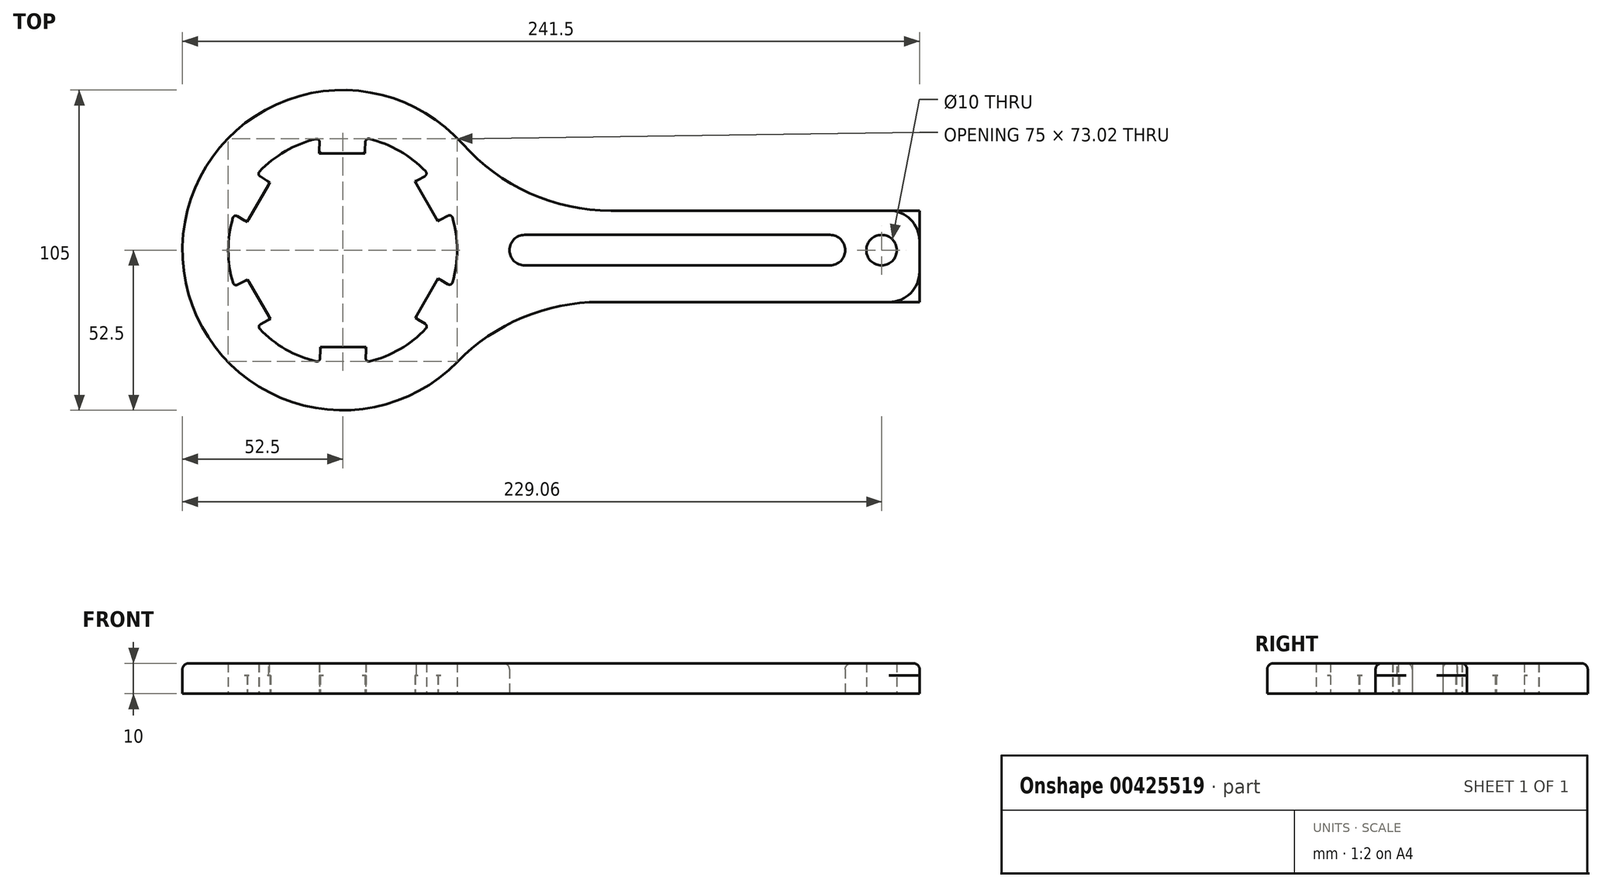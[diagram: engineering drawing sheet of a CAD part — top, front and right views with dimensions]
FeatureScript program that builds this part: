
annotation { "Feature Type Name" : "Feature", "Feature Type Description" : "" }
export const myFeature = defineFeature(function(context is Context, id is Id, definition is map)
    precondition{}
    {
        {
            var Q0;
            Q0=qCreatedBy(makeId("Top.planeOp"),FACE);
            var sketch = newSketch(context, id + "F0", { "sketchPlane" : qUnion([Q0])});
            skArc(sketch, "E0", {"start": v(-7.53, 36.74) * mm, "mid": v(-18.77, 32.46) * mm, "end": v(-28.09, 24.85) * mm});
            skArc(sketch, "E1", {"start": v(39.27, 34.84) * mm, "mid": v(-52.49, 1.23) * mm, "end": v(37.6, -36.65) * mm});
            skLineSegment(sketch, "E2.bottom", {"start": v(87.9, 12.98) * mm, "end": v(189, 12.98) * mm});
            skLineSegment(sketch, "E2.top", {"start": v(84.14, -17.02) * mm, "end": v(189, -17.02) * mm});
            skLineSegment(sketch, "E2.right", {"start": v(189, 12.98) * mm, "end": v(189, -17.02) * mm});
            skPoint(sketch, "E2.middle", {"position": v(118.24, 0) * mm});
            skPoint(sketch, "E3.visualSharp", {"position": v(50.87, 12.98) * mm});
            skArc(sketch, "E3.filletArc", {"start": v(39.27, 34.84) * mm, "mid": v(61.24, 18.7) * mm, "end": v(87.9, 12.98) * mm});
            skPoint(sketch, "E4.visualSharp", {"position": v(49.67, -17.02) * mm});
            skArc(sketch, "E4.filletArc", {"start": v(84.14, -17.02) * mm, "mid": v(58.88, -22.13) * mm, "end": v(37.6, -36.65) * mm});
            skLineSegment(sketch, "E5.bottom", {"start": v(7.3, 31.75) * mm, "end": v(-7.7, 31.74) * mm});
            skLineSegment(sketch, "E5.left", {"start": v(7.3, 31.75) * mm, "end": v(7.47, 36.75) * mm});
            skLineSegment(sketch, "E5.right", {"start": v(-7.7, 31.74) * mm, "end": v(-7.53, 36.74) * mm});
            skPoint(sketch, "E5.middle", {"position": v(0, 37.5) * mm});
            skPoint(sketch, "E5.top.end.orphan", {"position": v(-7.3, 43.25) * mm});
            skPoint(sketch, "E6.orphan", {"position": v(7.7, 43.26) * mm});
            skLineSegment(sketch, "E7.1.0", {"start": v(-31.34, 9.2) * mm, "end": v(-35.58, 11.85) * mm});
            skLineSegment(sketch, "E7.1.1", {"start": v(-23.84, 22.2) * mm, "end": v(-31.34, 9.2) * mm});
            skLineSegment(sketch, "E7.1.2", {"start": v(-23.84, 22.2) * mm, "end": v(-28.09, 24.85) * mm});
            skLineSegment(sketch, "E7.2.0", {"start": v(-23.64, -22.53) * mm, "end": v(-28.05, -24.89) * mm});
            skLineSegment(sketch, "E7.2.1", {"start": v(-31.15, -9.55) * mm, "end": v(-23.64, -22.53) * mm});
            skLineSegment(sketch, "E7.2.2", {"start": v(-31.15, -9.55) * mm, "end": v(-35.56, -11.9) * mm});
            skLineSegment(sketch, "E7.3.0", {"start": v(7.7, -31.74) * mm, "end": v(7.53, -36.74) * mm});
            skLineSegment(sketch, "E7.3.1", {"start": v(-7.3, -31.75) * mm, "end": v(7.7, -31.74) * mm});
            skLineSegment(sketch, "E7.3.2", {"start": v(-7.3, -31.75) * mm, "end": v(-7.47, -36.75) * mm});
            skLineSegment(sketch, "E7.4.0", {"start": v(31.34, -9.2) * mm, "end": v(35.58, -11.85) * mm});
            skLineSegment(sketch, "E7.4.1", {"start": v(23.84, -22.2) * mm, "end": v(31.34, -9.2) * mm});
            skLineSegment(sketch, "E7.4.2", {"start": v(23.84, -22.2) * mm, "end": v(28.09, -24.85) * mm});
            skLineSegment(sketch, "E7.5.0", {"start": v(23.64, 22.53) * mm, "end": v(28.05, 24.89) * mm});
            skLineSegment(sketch, "E7.5.1", {"start": v(31.15, 9.55) * mm, "end": v(23.64, 22.53) * mm});
            skLineSegment(sketch, "E7.5.2", {"start": v(31.15, 9.55) * mm, "end": v(35.56, 11.9) * mm});
            skArc(sketch, "E8.trimOffspring", {"start": v(28.05, 24.89) * mm, "mid": v(18.73, 32.49) * mm, "end": v(7.47, 36.75) * mm});
            skArc(sketch, "E9.trimOffspring", {"start": v(35.58, -11.85) * mm, "mid": v(37.5, 0.03) * mm, "end": v(35.56, 11.9) * mm});
            skArc(sketch, "E10.trimOffspring", {"start": v(-35.58, 11.85) * mm, "mid": v(-37.5, -0.03) * mm, "end": v(-35.56, -11.9) * mm});
            skArc(sketch, "E11.trimOffspring", {"start": v(-28.05, -24.89) * mm, "mid": v(-18.73, -32.49) * mm, "end": v(-7.47, -36.75) * mm});
            skArc(sketch, "E12.trimOffspring", {"start": v(7.53, -36.74) * mm, "mid": v(18.77, -32.46) * mm, "end": v(28.09, -24.85) * mm});
            skLineSegment(sketch, "E13", {"start": v(59.64, 0) * mm, "end": v(159.64, 0) * mm, "construction": true});
            skArc(sketch, "E14.0.startCap", {"start": v(59.64, -5) * mm, "mid": v(54.64, 0) * mm, "end": v(59.64, 5) * mm});
            skArc(sketch, "E14.0.endCap", {"start": v(159.64, 5) * mm, "mid": v(164.64, 0) * mm, "end": v(159.64, -5) * mm});
            skLineSegment(sketch, "E14.0.left", {"start": v(59.64, 5) * mm, "end": v(159.64, 5) * mm});
            skLineSegment(sketch, "E14.0.right", {"start": v(59.64, -5) * mm, "end": v(159.64, -5) * mm});
            skCircle(sketch, "E15", {"center": v(176.56, 0) * mm, "radius": 5 * mm});
            skSolve(sketch);
        }
        {
            var Q0;
            Q0=makeQuery(id+"F0.imprint","IMPRINT",FACE,{"disambiguationData":[TD([[makeQuery(id+"F0.imprint","IMPRINT",EDGE,{"derivedFrom":sQuery(id+"F0.wireOp",EDGE,"E0")}),-1.0]])]});
            extrude(context, id + "F1", {"entities" : qUnion([Q0]), "depth" : 10 * mm});
        }
        {
            var Q0;
            Q0=makeQuery(id+"F1.opExtrude","SWEPT_EDGE",EDGE,{"disambiguationData":[OSD([sQuery(id+"F0.wireOp",EDGE,"E2.bottom"),sQuery(id+"F0.wireOp",EDGE,"E2.right")])]});
            var Q1;
            Q1=makeQuery(id+"F1.opExtrude","SWEPT_EDGE",EDGE,{"disambiguationData":[OSD([sQuery(id+"F0.wireOp",EDGE,"E2.top"),sQuery(id+"F0.wireOp",EDGE,"E2.right")])]});
            fillet(context, id + "F2", {"entities" : qUnion([Q0, Q1]), "radius" : 10 * mm, "tangentPropagation" : true, "allowEdgeOverflow" : false});
        }
        {
            var Q0;
            Q0=makeQuery(id+"F1.opExtrude","SWEPT_EDGE",EDGE,{"disambiguationData":[OSD([sQuery(id+"F0.wireOp",EDGE,"E0"),sQuery(id+"F0.wireOp",EDGE,"E5.right")])]});
            var Q1;
            Q1=makeQuery(id+"F1.opExtrude","SWEPT_EDGE",EDGE,{"disambiguationData":[OSD([sQuery(id+"F0.wireOp",EDGE,"E5.bottom"),sQuery(id+"F0.wireOp",EDGE,"E5.right")])]});
            var Q2;
            Q2=makeQuery(id+"F1.opExtrude","SWEPT_EDGE",EDGE,{"disambiguationData":[OSD([sQuery(id+"F0.wireOp",EDGE,"E5.bottom"),sQuery(id+"F0.wireOp",EDGE,"E5.left")])]});
            var Q3;
            Q3=makeQuery(id+"F1.opExtrude","SWEPT_EDGE",EDGE,{"disambiguationData":[OSD([sQuery(id+"F0.wireOp",EDGE,"E5.left"),sQuery(id+"F0.wireOp",EDGE,"E8.trimOffspring")])]});
            var Q4;
            Q4=makeQuery(id+"F1.opExtrude","SWEPT_EDGE",EDGE,{"disambiguationData":[OSD([sQuery(id+"F0.wireOp",EDGE,"E7.5.0"),sQuery(id+"F0.wireOp",EDGE,"E7.5.1")])]});
            var Q5;
            Q5=makeQuery(id+"F1.opExtrude","SWEPT_EDGE",EDGE,{"disambiguationData":[OSD([sQuery(id+"F0.wireOp",EDGE,"E7.5.0"),sQuery(id+"F0.wireOp",EDGE,"E8.trimOffspring")])]});
            var Q6;
            Q6=makeQuery(id+"F1.opExtrude","SWEPT_EDGE",EDGE,{"disambiguationData":[OSD([sQuery(id+"F0.wireOp",EDGE,"E7.5.1"),sQuery(id+"F0.wireOp",EDGE,"E7.5.2")])]});
            var Q7;
            Q7=makeQuery(id+"F1.opExtrude","SWEPT_EDGE",EDGE,{"disambiguationData":[OSD([sQuery(id+"F0.wireOp",EDGE,"E7.5.2"),sQuery(id+"F0.wireOp",EDGE,"E9.trimOffspring")])]});
            var Q8;
            Q8=makeQuery(id+"F1.opExtrude","SWEPT_EDGE",EDGE,{"disambiguationData":[OSD([sQuery(id+"F0.wireOp",EDGE,"E7.4.0"),sQuery(id+"F0.wireOp",EDGE,"E9.trimOffspring")])]});
            var Q9;
            Q9=makeQuery(id+"F1.opExtrude","SWEPT_EDGE",EDGE,{"disambiguationData":[OSD([sQuery(id+"F0.wireOp",EDGE,"E7.4.0"),sQuery(id+"F0.wireOp",EDGE,"E7.4.1")])]});
            var Q10;
            Q10=makeQuery(id+"F1.opExtrude","SWEPT_EDGE",EDGE,{"disambiguationData":[OSD([sQuery(id+"F0.wireOp",EDGE,"E7.4.1"),sQuery(id+"F0.wireOp",EDGE,"E7.4.2")])]});
            var Q11;
            Q11=makeQuery(id+"F1.opExtrude","SWEPT_EDGE",EDGE,{"disambiguationData":[OSD([sQuery(id+"F0.wireOp",EDGE,"E7.4.2"),sQuery(id+"F0.wireOp",EDGE,"E12.trimOffspring")])]});
            var Q12;
            Q12=makeQuery(id+"F1.opExtrude","SWEPT_EDGE",EDGE,{"disambiguationData":[OSD([sQuery(id+"F0.wireOp",EDGE,"E7.3.0"),sQuery(id+"F0.wireOp",EDGE,"E12.trimOffspring")])]});
            var Q13;
            Q13=makeQuery(id+"F1.opExtrude","SWEPT_EDGE",EDGE,{"disambiguationData":[OSD([sQuery(id+"F0.wireOp",EDGE,"E7.3.0"),sQuery(id+"F0.wireOp",EDGE,"E7.3.1")])]});
            var Q14;
            Q14=makeQuery(id+"F1.opExtrude","SWEPT_EDGE",EDGE,{"disambiguationData":[OSD([sQuery(id+"F0.wireOp",EDGE,"E7.3.1"),sQuery(id+"F0.wireOp",EDGE,"E7.3.2")])]});
            var Q15;
            Q15=makeQuery(id+"F1.opExtrude","SWEPT_EDGE",EDGE,{"disambiguationData":[OSD([sQuery(id+"F0.wireOp",EDGE,"E7.3.2"),sQuery(id+"F0.wireOp",EDGE,"E11.trimOffspring")])]});
            var Q16;
            Q16=makeQuery(id+"F1.opExtrude","SWEPT_EDGE",EDGE,{"disambiguationData":[OSD([sQuery(id+"F0.wireOp",EDGE,"E7.2.0"),sQuery(id+"F0.wireOp",EDGE,"E11.trimOffspring")])]});
            var Q17;
            Q17=makeQuery(id+"F1.opExtrude","SWEPT_EDGE",EDGE,{"disambiguationData":[OSD([sQuery(id+"F0.wireOp",EDGE,"E7.2.0"),sQuery(id+"F0.wireOp",EDGE,"E7.2.1")])]});
            var Q18;
            Q18=makeQuery(id+"F1.opExtrude","SWEPT_EDGE",EDGE,{"disambiguationData":[OSD([sQuery(id+"F0.wireOp",EDGE,"E7.2.1"),sQuery(id+"F0.wireOp",EDGE,"E7.2.2")])]});
            var Q19;
            Q19=makeQuery(id+"F1.opExtrude","SWEPT_EDGE",EDGE,{"disambiguationData":[OSD([sQuery(id+"F0.wireOp",EDGE,"E7.2.2"),sQuery(id+"F0.wireOp",EDGE,"E10.trimOffspring")])]});
            var Q20;
            Q20=makeQuery(id+"F1.opExtrude","SWEPT_EDGE",EDGE,{"disambiguationData":[OSD([sQuery(id+"F0.wireOp",EDGE,"E7.1.0"),sQuery(id+"F0.wireOp",EDGE,"E10.trimOffspring")])]});
            var Q21;
            Q21=makeQuery(id+"F1.opExtrude","SWEPT_EDGE",EDGE,{"disambiguationData":[OSD([sQuery(id+"F0.wireOp",EDGE,"E7.1.0"),sQuery(id+"F0.wireOp",EDGE,"E7.1.1")])]});
            var Q22;
            Q22=makeQuery(id+"F1.opExtrude","SWEPT_EDGE",EDGE,{"disambiguationData":[OSD([sQuery(id+"F0.wireOp",EDGE,"E7.1.1"),sQuery(id+"F0.wireOp",EDGE,"E7.1.2")])]});
            var Q23;
            Q23=makeQuery(id+"F1.opExtrude","SWEPT_EDGE",EDGE,{"disambiguationData":[OSD([sQuery(id+"F0.wireOp",EDGE,"E0"),sQuery(id+"F0.wireOp",EDGE,"E7.1.2")])]});
            fillet(context, id + "F3", {"entities" : qUnion([Q0, Q1, Q2, Q3, Q4, Q5, Q6, Q7, Q8, Q9, Q10, Q11, Q12, Q13, Q14, Q15, Q16, Q17, Q18, Q19, Q20, Q21, Q22, Q23]), "radius" : 1 * mm, "tangentPropagation" : true, "allowEdgeOverflow" : false});
        }
        {
            var Q0;
            Q0=makeQuery(id+"F0.imprint","IMPRINT",FACE,{"disambiguationData":[TD([[makeQuery(id+"F0.imprint","IMPRINT",EDGE,{"derivedFrom":sQuery(id+"F0.wireOp",EDGE,"E14.0.startCap")}),-1.0]])]});
            extrude(context, id + "F4", {"entities" : qUnion([Q0]), "operationType" : NewBodyOperationType.ADD, "depth" : 6 * mm});
        }
        {
            var Q0;
            Q0=makeQuery(id+"F4.opExtrude","CAP_EDGE",EDGE,{"disambiguationData":[OSD([sQuery(id+"F0.wireOp",EDGE,"E14.0.left")])],"isStart":false});
            var Q1;
            Q1=makeQuery(id+"F1.opExtrude","CAP_EDGE",EDGE,{"disambiguationData":[OSD([sQuery(id+"F0.wireOp",EDGE,"E14.0.left")])],"isStart":false});
            fillet(context, id + "F5", {"entities" : qUnion([Q0, Q1]), "radius" : 2 * mm, "tangentPropagation" : true, "allowEdgeOverflow" : false});
        }
        {
            var Q0;
            Q0=makeQuery(id+"F1.opExtrude","CAP_EDGE",EDGE,{"disambiguationData":[OSD([sQuery(id+"F0.wireOp",EDGE,"E1")])],"isStart":false});
            fillet(context, id + "F6", {"entities" : qUnion([Q0]), "radius" : 2 * mm, "tangentPropagation" : true, "allowEdgeOverflow" : false});
        }
    });
